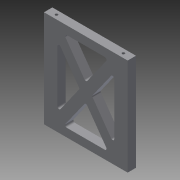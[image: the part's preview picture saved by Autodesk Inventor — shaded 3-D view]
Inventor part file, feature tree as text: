
AUTODESK INVENTOR PART (.ipt)
format: ipt  version: 2013 (Build 170138000, 138)  size: 143,360 bytes
history: native  units: mm
features: sketch x3, extrude x2, hole x1, fillet x1
ambient origin geometry x8: Origin, YZ Plane, XZ Plane, XY Plane, X Axis, Y Axis, Z Axis, Center Point
feature tree (7):
  extrude  "押し出し2"  Depth=50.0mm
  hole  "穴1"  [1 undecoded]
  extrude  "押し出し3"  Depth=25.0mm
  fillet  "フィレット1"  Radius=5.0mm
  sketch  "スケッチ1"
  sketch  "スケッチ2"
  sketch  "スケッチ3"
note: 1 required parameter value undecoded (feature->parameter linkage not recoverable at this tier; creation-order binding heuristic only, values carry confidence <= 0.55)
